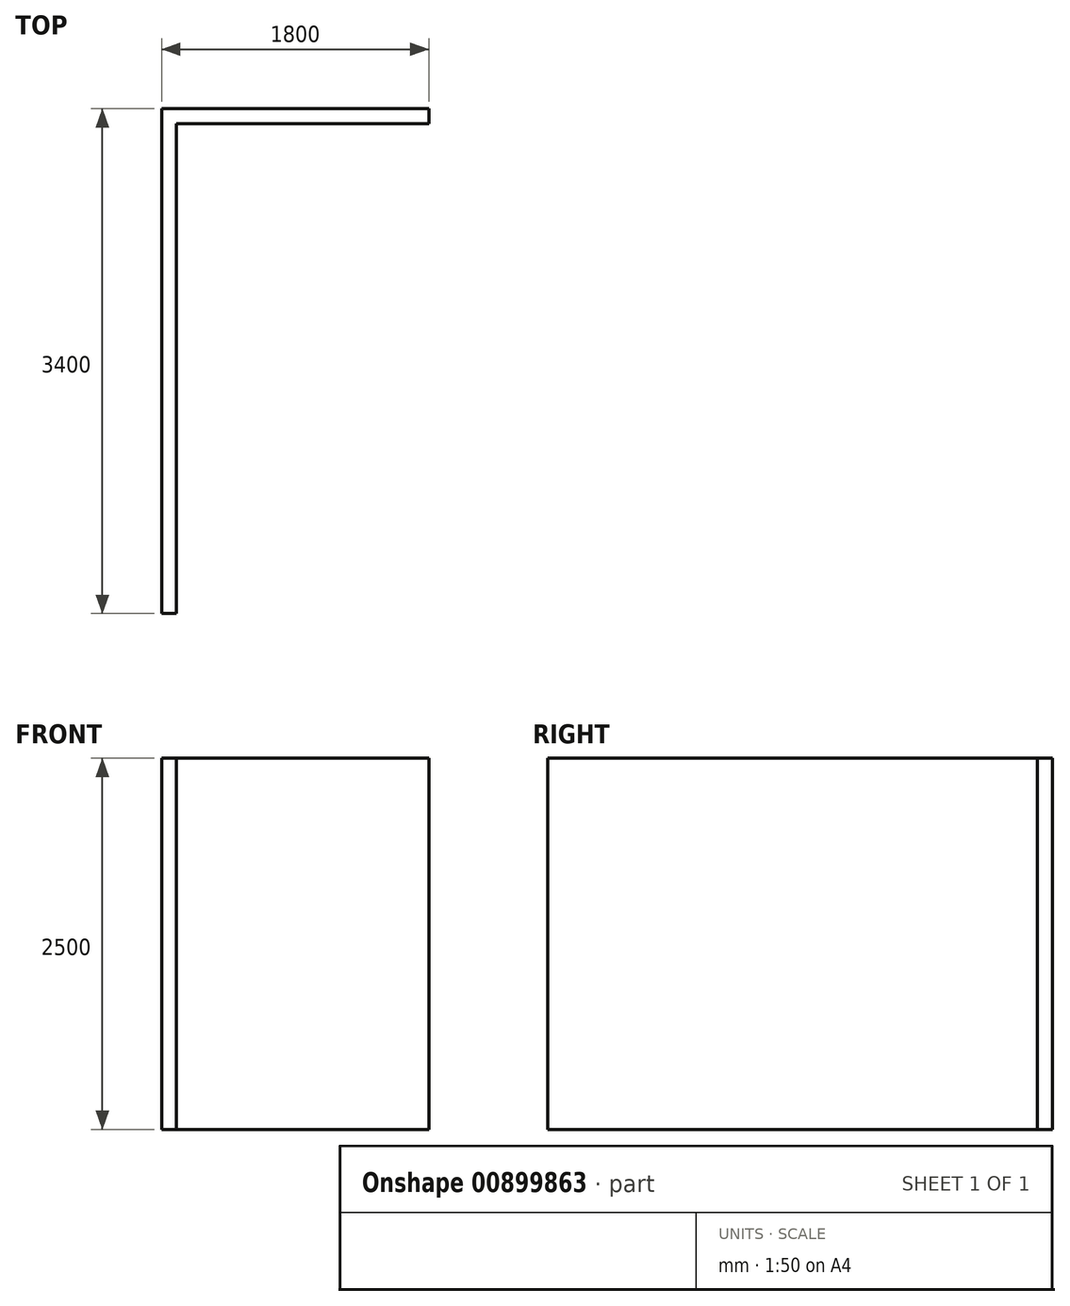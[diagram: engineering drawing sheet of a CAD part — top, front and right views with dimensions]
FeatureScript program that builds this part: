
annotation { "Feature Type Name" : "Feature", "Feature Type Description" : "" }
export const myFeature = defineFeature(function(context is Context, id is Id, definition is map)
    precondition{}
    {
        {
            var Q0;
            Q0=qCreatedBy(makeId("Top.planeOp"),FACE);
            var sketch = newSketch(context, id + "F0", { "sketchPlane" : qUnion([Q0])});
            skLineSegment(sketch, "E0.bottom", {"start": v(0, 0) * mm, "end": v(-100, 0) * mm});
            skLineSegment(sketch, "E0.top", {"start": v(0, -3300) * mm, "end": v(-100, -3300) * mm});
            skLineSegment(sketch, "E0.left", {"start": v(0, 0) * mm, "end": v(0, -3300) * mm});
            skLineSegment(sketch, "E0.right", {"start": v(-100, 0) * mm, "end": v(-100, -3300) * mm});
            skLineSegment(sketch, "E1.bottom", {"start": v(-100, 0) * mm, "end": v(1700, 0) * mm});
            skLineSegment(sketch, "E1.top", {"start": v(-100, 100) * mm, "end": v(1700, 100) * mm});
            skLineSegment(sketch, "E1.left", {"start": v(-100, 0) * mm, "end": v(-100, 100) * mm});
            skLineSegment(sketch, "E1.right", {"start": v(1700, 0) * mm, "end": v(1700, 100) * mm});
            skSolve(sketch);
        }
        {
            var Q0;
            Q0 = qSketchRegion(id + "F0", true);
            extrude(context, id + "F1", {"entities" : qUnion([Q0]), "depth" : 2500 * mm, "offsetDistance" : 25 * mm});
        }
    });
